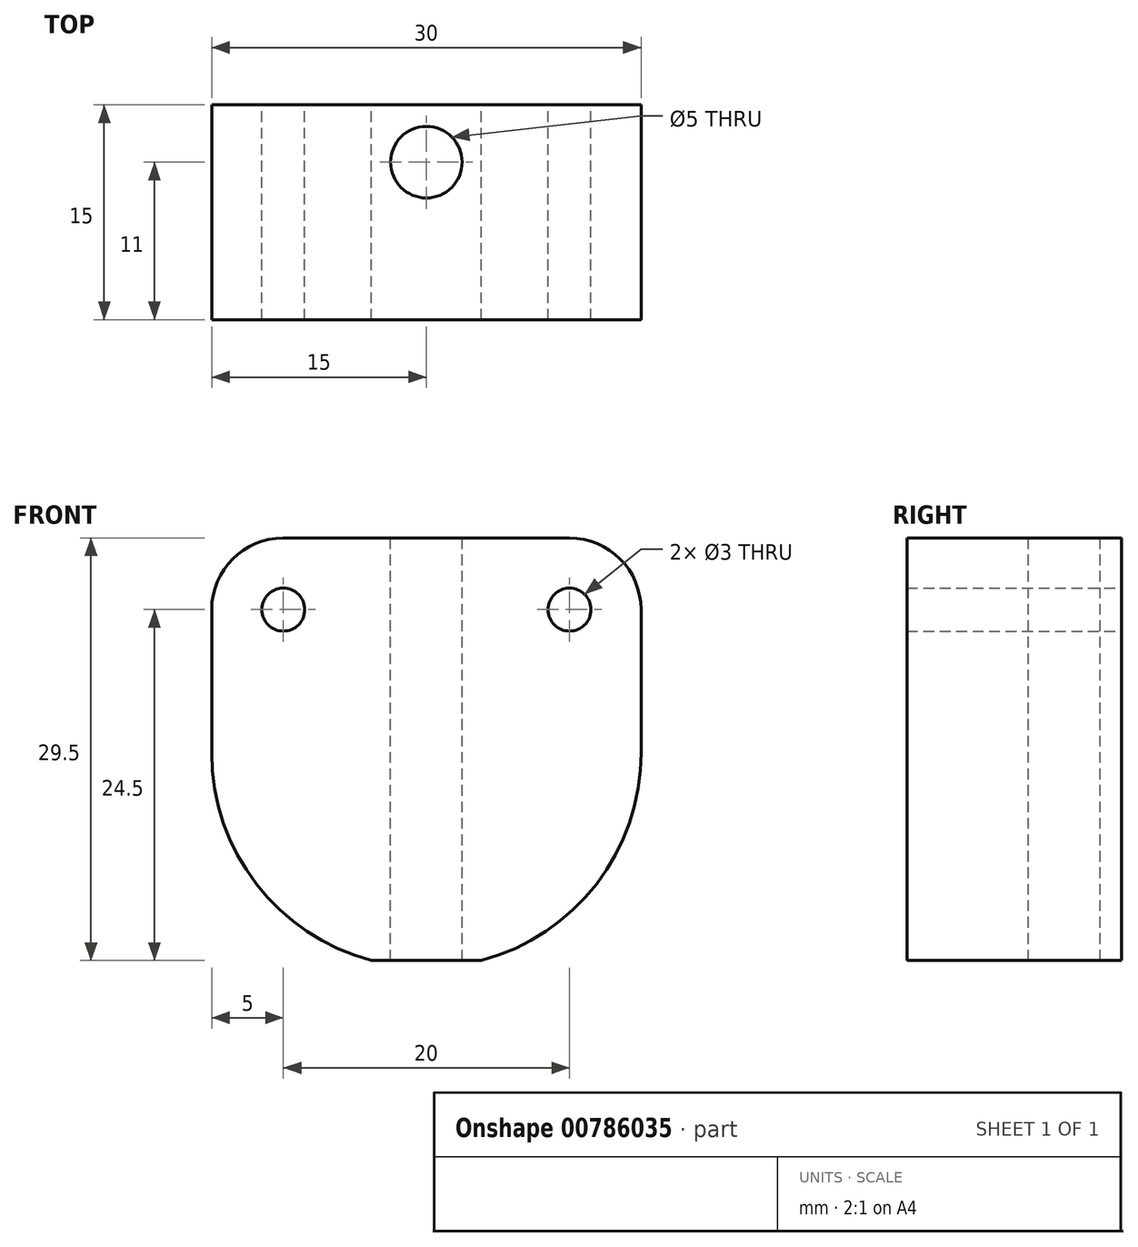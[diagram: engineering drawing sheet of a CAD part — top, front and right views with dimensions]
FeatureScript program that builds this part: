
annotation { "Feature Type Name" : "Feature", "Feature Type Description" : "" }
export const myFeature = defineFeature(function(context is Context, id is Id, definition is map)
    precondition{}
    {
        {
            var Q0;
            Q0=qCreatedBy(makeId("Front.planeOp"),FACE);
            var sketch = newSketch(context, id + "F0", { "sketchPlane" : qUnion([Q0])});
            skLineSegment(sketch, "E0.bottom", {"start": v(15, 15) * mm, "end": v(-15, 15) * mm});
            skLineSegment(sketch, "E0.top", {"start": v(15, -15) * mm, "end": v(-15, -15) * mm});
            skLineSegment(sketch, "E0.left", {"start": v(15, 15) * mm, "end": v(15, -15) * mm});
            skLineSegment(sketch, "E0.right", {"start": v(-15, 15) * mm, "end": v(-15, -15) * mm});
            skPoint(sketch, "E0.middle", {"position": v(0, 0) * mm});
            skCircle(sketch, "E1", {"center": v(0, 0) * mm, "radius": 15 * mm});
            skLineSegment(sketch, "E2", {"start": v(3.84, -14.5) * mm, "end": v(-3.84, -14.5) * mm});
            skSolve(sketch);
        }
        {
            var Q0;
            {var subQ0=sQuery(id+"F0.wireOp",EDGE,"E0.left");var subQ1=sQuery(id+"F0.wireOp",EDGE,"E0.bottom");var subQ2=makeQuery(id+"F0.imprint","INTERSECT",VERTEX,{"derivedFrom":[subQ1,subQ0]});Q0=makeQuery(id+"F0.imprint","IMPRINT",FACE,{"disambiguationData":[TD([[makeQuery(id+"F0.imprint","IMPRINT",EDGE,{"disambiguationData":[TD([[subQ2,-1.0]])],"derivedFrom":subQ1}),1.0]])]});}
            var Q1;
            {var subQ0=sQuery(id+"F0.wireOp",EDGE,"E0.right");var subQ1=sQuery(id+"F0.wireOp",EDGE,"E0.bottom");var subQ2=makeQuery(id+"F0.imprint","INTERSECT",VERTEX,{"derivedFrom":[subQ1,subQ0]});Q1=makeQuery(id+"F0.imprint","IMPRINT",FACE,{"disambiguationData":[TD([[makeQuery(id+"F0.imprint","IMPRINT",EDGE,{"disambiguationData":[TD([[subQ2,1.0]])],"derivedFrom":subQ1}),1.0]])]});}
            var Q2;
            {var subQ0=sQuery(id+"F0.wireOp",EDGE,"E1");var subQ1=makeQuery(id+"F0.imprint","INTERSECT",VERTEX,{"derivedFrom":[sQuery(id+"F0.wireOp",EDGE,"E0.bottom"),subQ0]});Q2=makeQuery(id+"F0.imprint","IMPRINT",FACE,{"disambiguationData":[TD([[makeQuery(id+"F0.imprint","IMPRINT",EDGE,{"disambiguationData":[TD([[subQ1,1.0]])],"derivedFrom":subQ0}),1.0]])]});}
            extrude(context, id + "F1", {"entities" : qUnion([Q0, Q1, Q2]), "depth" : 15 * mm, "offsetDistance" : 25 * mm});
        }
        {
            var Q0;
            Q0=makeQuery(id+"F1.opExtrude","CAP_FACE",FACE,{"disambiguationData":[OSD([sQuery(id+"F0.wireOp",EDGE,"E0.bottom"),sQuery(id+"F0.wireOp",EDGE,"E0.left"),sQuery(id+"F0.wireOp",EDGE,"E0.right"),sQuery(id+"F0.wireOp",EDGE,"E1"),sQuery(id+"F0.wireOp",EDGE,"E2")])],"isStart":true});
            var sketch = newSketch(context, id + "F2", { "sketchPlane" : qUnion([Q0])});
            skCircle(sketch, "E3", {"center": v(10, 10) * mm, "radius": 1.5 * mm});
            skCircle(sketch, "E4", {"center": v(-10, 10) * mm, "radius": 1.5 * mm});
            skSolve(sketch);
        }
        {
            var Q0;
            Q0=makeQuery(id+"F2.imprint","IMPRINT",FACE,{"disambiguationData":[TD([[makeQuery(id+"F2.imprint","IMPRINT",EDGE,{"derivedFrom":sQuery(id+"F2.wireOp",EDGE,"E3")}),1.0]])]});
            var Q1;
            Q1=makeQuery(id+"F2.imprint","IMPRINT",FACE,{"disambiguationData":[TD([[makeQuery(id+"F2.imprint","IMPRINT",EDGE,{"derivedFrom":sQuery(id+"F2.wireOp",EDGE,"E4")}),1.0]])]});
            extrude(context, id + "F3", {"entities" : qUnion([Q0, Q1]), "operationType" : NewBodyOperationType.REMOVE, "oppositeDirection" : true, "depth" : 25 * mm, "offsetDistance" : 25 * mm});
        }
        {
            var Q0;
            Q0=makeQuery(id+"F1.opExtrude","SWEPT_EDGE",EDGE,{"disambiguationData":[OSD([sQuery(id+"F0.wireOp",EDGE,"E0.bottom"),sQuery(id+"F0.wireOp",EDGE,"E0.right")])]});
            var Q1;
            Q1=makeQuery(id+"F1.opExtrude","SWEPT_EDGE",EDGE,{"disambiguationData":[OSD([sQuery(id+"F0.wireOp",EDGE,"E0.bottom"),sQuery(id+"F0.wireOp",EDGE,"E0.left")])]});
            fillet(context, id + "F4", {"entities" : qUnion([Q0, Q1]), "radius" : 5 * mm, "tangentPropagation" : true, "allowEdgeOverflow" : false});
        }
        {
            var Q0;
            Q0=makeQuery(id+"F1.opExtrude","SWEPT_FACE",FACE,{"disambiguationData":[OSD([sQuery(id+"F0.wireOp",EDGE,"E0.bottom")])]});
            var sketch = newSketch(context, id + "F5", { "sketchPlane" : qUnion([Q0])});
            skCircle(sketch, "E5", {"center": v(0, -4) * mm, "radius": 2.5 * mm});
            skPoint(sketch, "E5.centerSnap0", {"position": v(0, 0) * mm});
            skSolve(sketch);
        }
        {
            var Q0;
            Q0=qSketchRegion(id+"F5",true);
            extrude(context, id + "F6", {"entities" : qUnion([Q0]), "operationType" : NewBodyOperationType.REMOVE, "endBound" : BoundingType.THROUGH_ALL, "oppositeDirection" : true, "depth" : 25 * mm, "offsetDistance" : 25 * mm});
        }
    });
